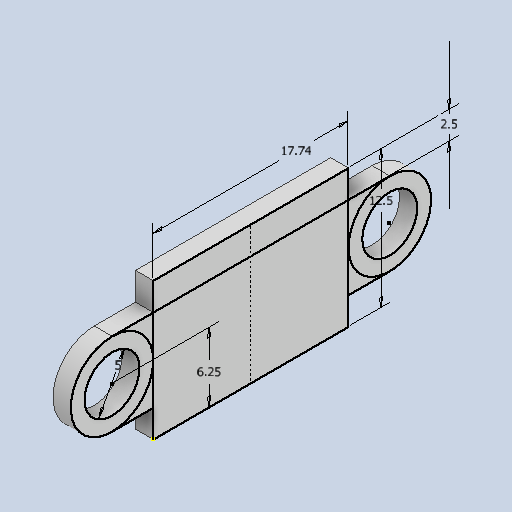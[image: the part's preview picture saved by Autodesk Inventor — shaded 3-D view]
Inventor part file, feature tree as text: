
AUTODESK INVENTOR PART (.ipt)
format: ipt  version: 2022 (Build 260153070, 153G)  size: 123,904 bytes
history: native  units: in
note: dims shown in document units (in); Inventor stores cm internally (conversion verified against a paired STEP export)
features: sketch x1, extrude x1
ambient origin geometry x8: Origin, YZ Plane, XZ Plane, XY Plane, X Axis, Y Axis, Z Axis, Center Point
bodies: Solid1 (feature_tree)
feature tree (2):
  sketch  "Sketch1"  dims[d0=0.6984in d1=0.4921in d2=0.2461in d3=0.1969in d4=0.0984in d7=0.0618in d8=0.0in]
  extrude  "Extrusion1"  Depth=0.4921in
